# Revit family: Shinhoo_INSTANT
name_source: partatom
category: Оборудование
units: mm (PartAtom-declared; Revit-internal decimal feet)

## family parameters
Всегда вертикально = Нет
Классификация = Нет
На основе рабочей плоскости = Нет
Общий = Нет
При загрузке вырезать с полостями = Нет
Размер круглого соединителя = Использовать диаметр
Тип детали = Вставляется
Точка расчета площади = Нет

## types (1)
- INSTANT 15-1.5 II BL - 71311001
    ADSK_URL страницы изделия = https://shinhoopump.ru
    ADSK_Версия Revit = 2019
    ADSK_Версия семейства = 1.0
    ADSK_Единица измерения = шт
    ADSK_Завод-изготовитель = Shinhoo
    ADSK_Код изделия = 71311001
    ADSK_Количество = 1
    ADSK_Коэффициент мощности = 1
    ADSK_Масса = 1
    ADSK_Масса_Текст = 1
    ADSK_Материал = Коррозионностойкая латунь
    ADSK_Наименование = Циркуляционный насос для систем ГВС с «мокрым» ротором INSTANT 15-1.5 II BL
    ADSK_Наименование краткое = INSTANT 15-1.5 II BL
    ADSK_Напряжение = 230 В
    ADSK_Номинальная мощность = 5 Вт
    ADSK_Обозначение = ГОСТ 31839-2012, ГОСТ 12.2.007.0-75, ГОСТ 12.2.003-91, ГОСТ Р МЭК 60204-1-2007,  ГОСТ 30804
    ADSK_Полная мощность = 5 В·А
    ADSK_Расход жидкости = 0.000250 м³/с
    ADSK_Ток = 0 А
    B = 77 мм
    B1 = 39 мм
    B2 = 39 мм
    DN = 15 мм
    H = 112 мм
    H1 = 13 мм
    H2 = 99 мм
    L = 80 мм
    URL = https://shinhoopump.ru
    b1_20 = 33 мм
    d1 = 13 мм
    d6 = 26 мм
    r1 = 7 мм
    r1_1 = 8 мм
    r1_3 = 10 мм
    r6 = 13 мм
    Группа модели = INSTANT 15-1.5 II BL
    Изготовитель = Shinhoo
    Класс защиты (IP) = IP44
    Разработчик = ООО ПРОРУБИМ
    Разработчик (телефон) = +7(495)649-85-43
    Скорость вращения = 2850
    Степень защиты от удара (IK) = IK04
    Тип Насоса = Циркуляционный насос для систем ГВС с «мокрым» ротором
    Тип основания = встроенный

## geometry (parser evidence)
native form markers: Sweep x2
no freeform markers — native parametric forms only
